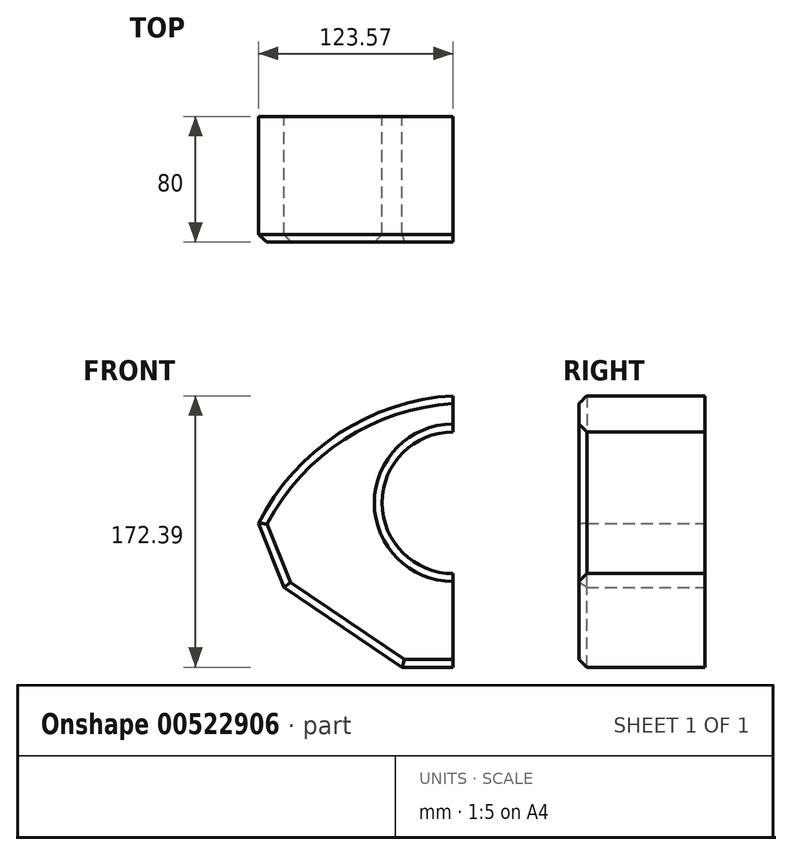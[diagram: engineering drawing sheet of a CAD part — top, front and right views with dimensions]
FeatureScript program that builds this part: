
annotation { "Feature Type Name" : "Feature", "Feature Type Description" : "" }
export const myFeature = defineFeature(function(context is Context, id is Id, definition is map)
    precondition{}
    {
        {
            var Q0;
            Q0=qCreatedBy(makeId("Front.planeOp"),FACE);
            var sketch = newSketch(context, id + "F0", { "sketchPlane" : qUnion([Q0])});
            skArc(sketch, "E0", {"start": v(0, 81.1) * mm, "mid": v(-72.6, 57.02) * mm, "end": v(-123.57, 0) * mm});
            skLineSegment(sketch, "E1", {"start": v(-123.57, 0) * mm, "end": v(-107.2, -40.63) * mm});
            skLineSegment(sketch, "E2", {"start": v(-107.2, -40.63) * mm, "end": v(-32.44, -91.3) * mm});
            skLineSegment(sketch, "E3", {"start": v(-32.44, -91.3) * mm, "end": v(0, -91.3) * mm});
            skLineSegment(sketch, "E4", {"start": v(0, -91.3) * mm, "end": v(0, 81.1) * mm});
            skArc(sketch, "E5.MirrorCS", {"start": v(0, 81.1) * mm, "mid": v(72.6, 57.02) * mm, "end": v(123.57, 0) * mm});
            skLineSegment(sketch, "E6.MirrorCS", {"start": v(123.57, 0) * mm, "end": v(107.2, -40.63) * mm});
            skLineSegment(sketch, "E7.MirrorCS", {"start": v(107.2, -40.63) * mm, "end": v(32.44, -91.3) * mm});
            skLineSegment(sketch, "E8.MirrorCS", {"start": v(32.44, -91.3) * mm, "end": v(0, -91.3) * mm});
            skCircle(sketch, "E9", {"center": v(0, 13.13) * mm, "radius": 45 * mm});
            skSolve(sketch);
        }
        {
            var Q0;
            {var subQ1=sQuery(id+"F0.wireOp",EDGE,"E0");Q0=makeQuery(id+"F0.imprint","IMPRINT",FACE,{"disambiguationData":[TD([[makeQuery(id+"F0.imprint","IMPRINT",EDGE,{"derivedFrom":subQ1}),1.0]])]});}
            var Q1;
            {var subQ0=sQuery(id+"F0.wireOp",EDGE,"E5.MirrorCS");Q1=makeQuery(id+"F0.imprint","IMPRINT",FACE,{"disambiguationData":[TD([[makeQuery(id+"F0.imprint","IMPRINT",EDGE,{"derivedFrom":subQ0}),-1.0]])]});}
            extrude(context, id + "F1", {"entities" : qUnion([Q0, Q1]), "depth" : 80 * mm, "offsetDistance" : 25 * mm});
        }
        {
            var Q0;
            Q0=makeQuery(id+"F1.opExtrude","CAP_EDGE",EDGE,{"disambiguationData":[OSD([sQuery(id+"F0.wireOp",EDGE,"E9")])],"isStart":false});
            var Q1;
            Q1=makeQuery(id+"F1.opExtrude","CAP_EDGE",EDGE,{"disambiguationData":[OSD([sQuery(id+"F0.wireOp",EDGE,"E5.MirrorCS")])],"isStart":false});
            var Q2;
            Q2=makeQuery(id+"F1.opExtrude","CAP_EDGE",EDGE,{"disambiguationData":[OSD([sQuery(id+"F0.wireOp",EDGE,"E6.MirrorCS")])],"isStart":false});
            var Q3;
            Q3=makeQuery(id+"F1.opExtrude","CAP_EDGE",EDGE,{"disambiguationData":[OSD([sQuery(id+"F0.wireOp",EDGE,"E7.MirrorCS")])],"isStart":false});
            var Q4;
            Q4=makeQuery(id+"F1.opExtrude","CAP_EDGE",EDGE,{"disambiguationData":[OSD([sQuery(id+"F0.wireOp",EDGE,"E0")])],"isStart":false});
            var Q5;
            Q5=makeQuery(id+"F1.opExtrude","CAP_EDGE",EDGE,{"disambiguationData":[OSD([sQuery(id+"F0.wireOp",EDGE,"E1")])],"isStart":false});
            var Q6;
            Q6=makeQuery(id+"F1.opExtrude","CAP_EDGE",EDGE,{"disambiguationData":[OSD([sQuery(id+"F0.wireOp",EDGE,"E2")])],"isStart":false});
            var Q7;
            Q7=makeQuery(id+"F1.opExtrude","CAP_EDGE",EDGE,{"disambiguationData":[OSD([sQuery(id+"F0.wireOp",EDGE,"E3"),sQuery(id+"F0.wireOp",EDGE,"E8.MirrorCS")])],"isStart":false});
            chamfer(context, id + "F2", {"entities" : qUnion([Q0, Q1, Q2, Q3, Q4, Q5, Q6, Q7]), "width" : 5 * mm, "tangentPropagation" : true});
        }
    });
